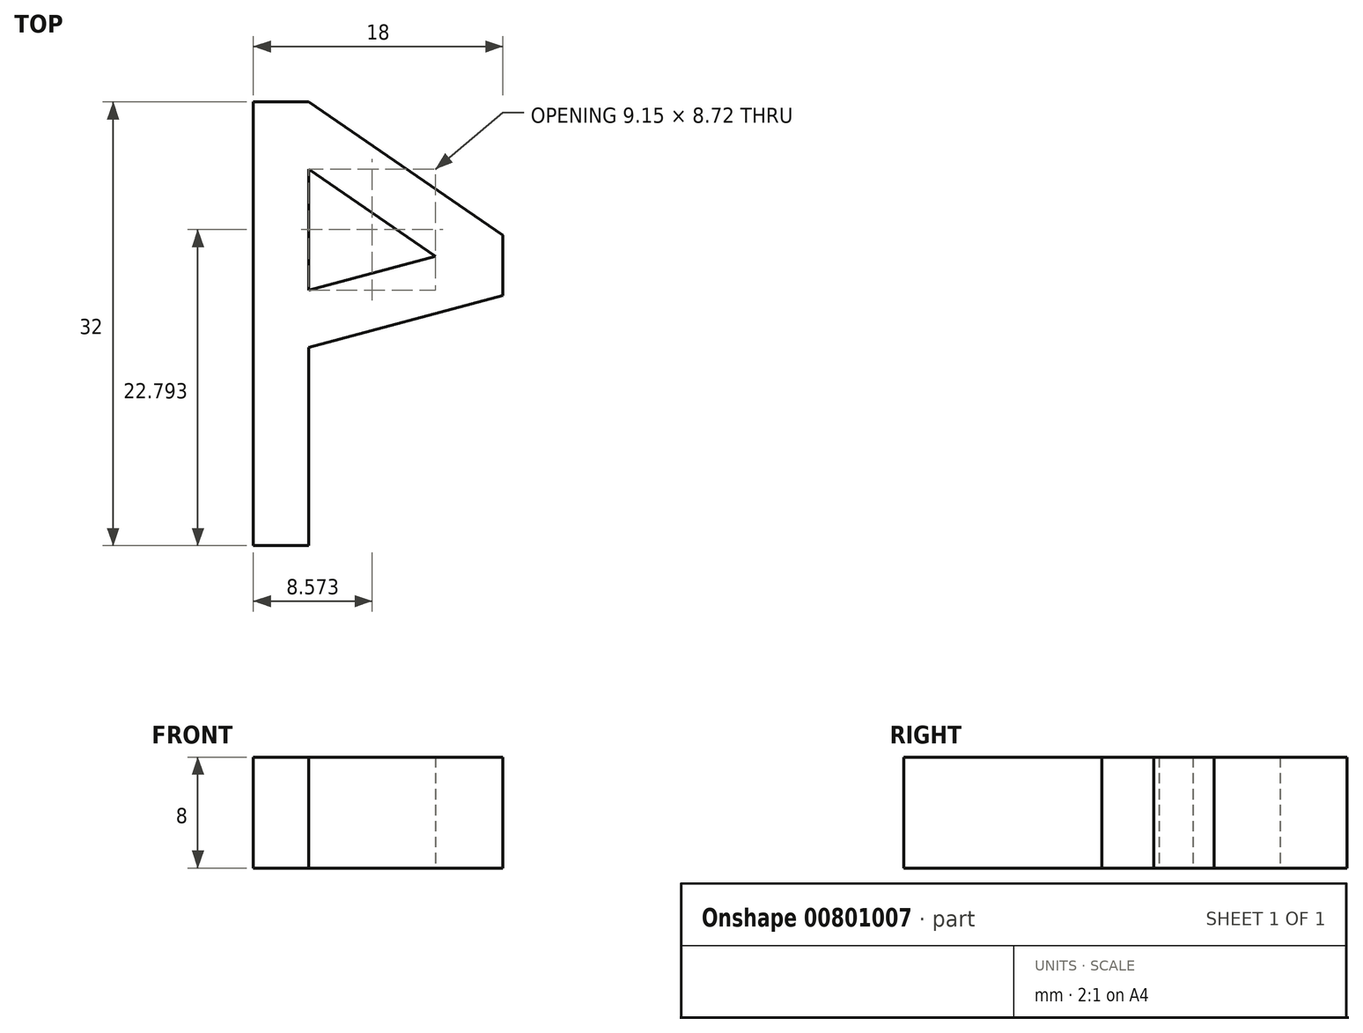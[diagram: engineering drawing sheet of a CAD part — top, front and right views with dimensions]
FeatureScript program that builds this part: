
annotation { "Feature Type Name" : "Feature", "Feature Type Description" : "" }
export const myFeature = defineFeature(function(context is Context, id is Id, definition is map)
    precondition{}
    {
        {
            var Q0;
            Q0=qCreatedBy(makeId("Top.planeOp"),FACE);
            var sketch = newSketch(context, id + "F0", { "sketchPlane" : qUnion([Q0])});
            skLineSegment(sketch, "E0", {"start": v(0, 0) * mm, "end": v(0, -32) * mm});
            skLineSegment(sketch, "E1", {"start": v(0, -32) * mm, "end": v(4, -32) * mm});
            skLineSegment(sketch, "E2", {"start": v(4, -32) * mm, "end": v(4, -22.83) * mm});
            skLineSegment(sketch, "E3", {"start": v(4, 0) * mm, "end": v(0, 0) * mm});
            skLineSegment(sketch, "E4", {"start": v(4, -4.85) * mm, "end": v(4, -13.57) * mm});
            skLineSegment(sketch, "E5", {"start": v(4, -13.57) * mm, "end": v(13.15, -11.12) * mm});
            skLineSegment(sketch, "E6", {"start": v(13.15, -11.12) * mm, "end": v(4, -4.85) * mm});
            skLineSegment(sketch, "E7", {"start": v(4, 0) * mm, "end": v(18, -9.6) * mm});
            skLineSegment(sketch, "E8", {"start": v(18, -9.6) * mm, "end": v(18, -13.96) * mm});
            skLineSegment(sketch, "E9", {"start": v(18, -13.96) * mm, "end": v(4, -17.7) * mm});
            skLineSegment(sketch, "E10", {"start": v(4, -17.7) * mm, "end": v(4, -22.83) * mm});
            skSolve(sketch);
        }
        {
            var Q0;
            Q0=makeQuery(id+"F0.imprint","IMPRINT",FACE,{"disambiguationData":[TD([[makeQuery(id+"F0.imprint","IMPRINT",EDGE,{"derivedFrom":sQuery(id+"F0.wireOp",EDGE,"E0")}),1.0]])]});
            extrude(context, id + "F1", {"entities" : qUnion([Q0]), "depth" : 8 * mm, "offsetDistance" : 25 * mm});
        }
    });
